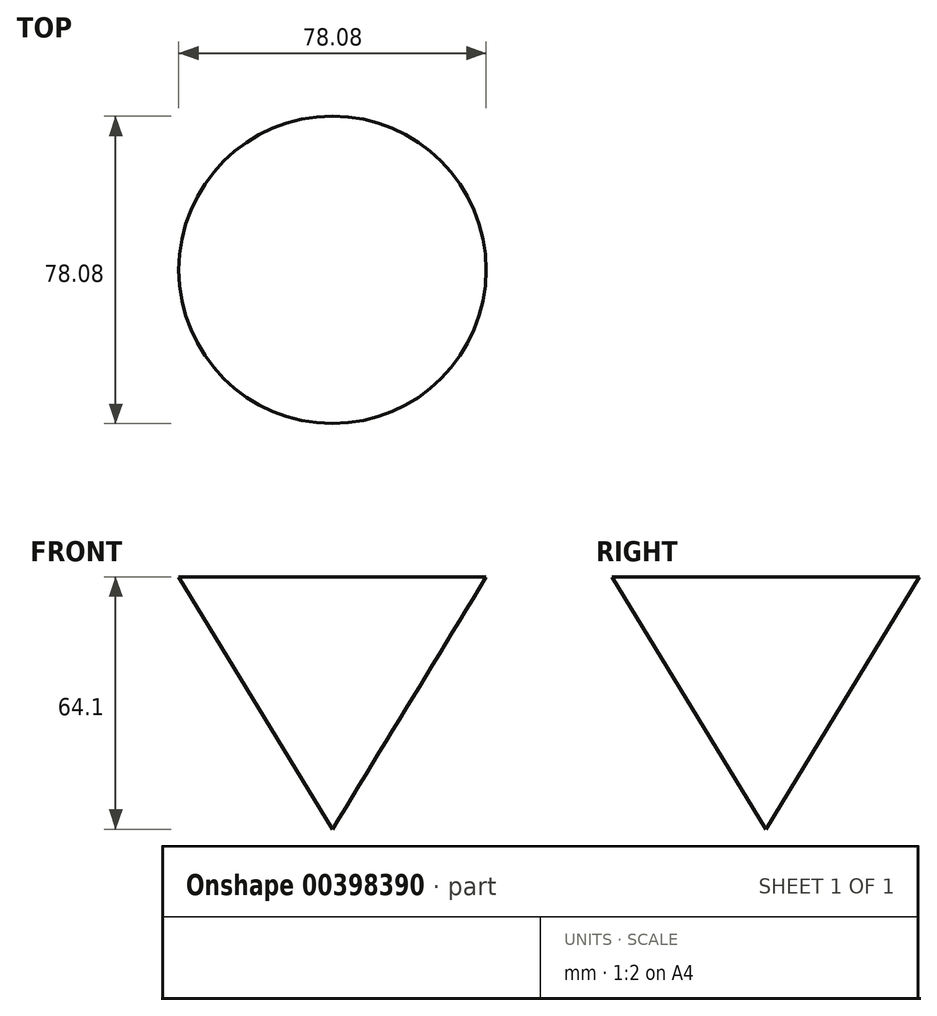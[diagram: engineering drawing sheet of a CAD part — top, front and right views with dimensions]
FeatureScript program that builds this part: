
annotation { "Feature Type Name" : "Feature", "Feature Type Description" : "" }
export const myFeature = defineFeature(function(context is Context, id is Id, definition is map)
    precondition{}
    {
        {
            var Q0;
            Q0=qCreatedBy(makeId("Right.planeOp"),FACE);
            var sketch = newSketch(context, id + "F0", { "sketchPlane" : qUnion([Q0])});
            skLineSegment(sketch, "E0", {"start": v(0, 32.05) * mm, "end": v(0, -32.05) * mm});
            skLineSegment(sketch, "E1", {"start": v(0, 32.05) * mm, "end": v(-39.04, 32.05) * mm});
            skLineSegment(sketch, "E2", {"start": v(-39.04, 32.05) * mm, "end": v(0, -32.05) * mm});
            skSolve(sketch);
        }
        {
            var Q0;
            Q0=makeQuery(id+"F0.imprint","IMPRINT",FACE,{"disambiguationData":[TD([[makeQuery(id+"F0.imprint","IMPRINT",EDGE,{"derivedFrom":sQuery(id+"F0.wireOp",EDGE,"E0")}),-1.0]])]});
            var Q1;
            Q1=sQuery(id+"F0.wireOp",EDGE,"E0");
            revolve(context, id + "F1", {"entities" : qUnion([Q0]), "axis" : qUnion([Q1]), "revolveType" : RevolveType.FULL});
        }
    });
